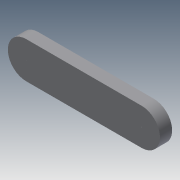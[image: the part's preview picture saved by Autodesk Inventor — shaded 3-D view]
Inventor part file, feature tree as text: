
AUTODESK INVENTOR PART (.ipt)
format: ipt  version: 2013 (Build 170138000, 138)  size: 76,800 bytes
history: native  units: mm
features: extrude x1, sketch x1
ambient origin geometry x8: Origin, YZ Plane, XZ Plane, XY Plane, X Axis, Y Axis, Z Axis, Center Point
bodies: Solid1 (feature_tree)
feature tree (2):
  extrude  "Extrusion1"  Depth=6.0mm
  sketch  "Sketch1"  dims[d0=19.0mm d1=6.0mm d2=0.1mm d3=0.1mm d4=2.0mm d5=0.0mm]
